# Revit family: Faucet-Wall_Mount-Lavatory-KOHLER-Taut-K-74027M
name_source: partatom
category: Plumbing Fixtures
units: mm (PartAtom-declared; Revit-internal decimal feet)

## family parameters
Cut with Voids When Loaded = No
Host = Face
OmniClass Number = 23.31.11.00
OmniClass Title = Faucets
Part Type = Normal
Room Calculation Point = No
Round Connector Dimension = Use Diameter
Shared = No

## types (3) — shared parameters
ADA Compliant = No
Assembly Code = D2010
CW Connection = Yes
Cold Water Inlet = Cold Water Inlet
Date Modified = 01/31/2023
Default Elevation = 36"
Flow Rate = 1 GPM
HW Connection = Yes
Handle Clearance = 3 1/16"
Height = 2 3/4"
Hot Water Inlet = Hot Water Inlet
Length = 7 7/8"
Manufacturer = Kohler Co.
Master Format 2014 = 22 41 39
Master Format 2014 Name = Residential Faucets, Supplies, and Trim
Material = Premium Metal Construction
Pressure = 43.51 psi
Product Name = Taut
Spout Reach = 7 7/8"
URL = https://la.kohler.com
Vent Connection = No
Waste Connection = No
Waste Water Outlet = Waste Water Outlet
WaterSense Certified = No
Width = 2 3/4"

## per-type parameters (varying)
| type | Description | Drain Included | Finish | Model | Product Documentation Link | Product Page URL | Type |
| With Drain, CP-Polished Chrome | Single Lever Wall Mount Lavatory Faucet | Yes | Kohler-Metal-CP-Polished_Chrome | K-74027M-4E2-CP |  |  | 1 |
| With Drain, BL-Matte Black | Single Lever Wall Mount Lavatory Faucet | Yes | Kohler-Metal-BL-Matte_Black | K-74027M-4E2-BL |  |  | 2 |
| Without Drain, CP-Polished Chrome | Single lever faucets for washbasin, wall mount | No | Kohler-Metal-CP-Polished_Chrome | K-74027M-4ND-CP | https://resources.kohler.com | https://la.kohler.com | 3 |

## geometry (parser evidence)
native form markers: Sweep x6
no freeform markers — native parametric forms only
